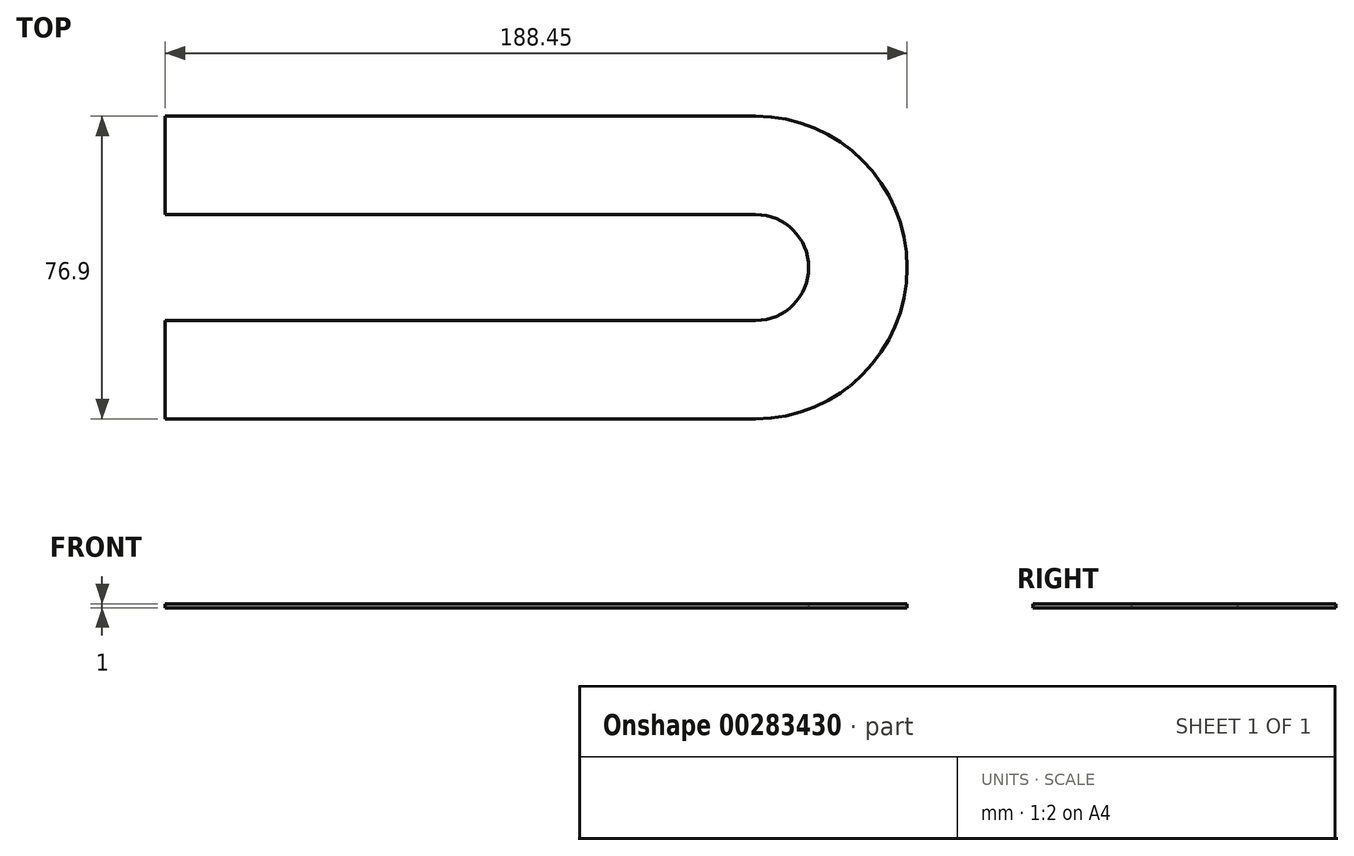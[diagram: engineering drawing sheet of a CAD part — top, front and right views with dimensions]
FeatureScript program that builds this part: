
annotation { "Feature Type Name" : "Feature", "Feature Type Description" : "" }
export const myFeature = defineFeature(function(context is Context, id is Id, definition is map)
    precondition{}
    {
        {
            var Q0;
            Q0=qCreatedBy(makeId("Top.planeOp"),FACE);
            var sketch = newSketch(context, id + "F0", { "sketchPlane" : qUnion([Q0])});
            skCircle(sketch, "E0", {"center": v(0, 0) * mm, "radius": 13.45 * mm});
            skLineSegment(sketch, "E1", {"start": v(0, 13.45) * mm, "end": v(-150, 13.45) * mm});
            skLineSegment(sketch, "E2", {"start": v(-150, 13.45) * mm, "end": v(-150, -13.45) * mm});
            skLineSegment(sketch, "E3", {"start": v(-150, -13.45) * mm, "end": v(0, -13.45) * mm});
            skLineSegment(sketch, "E4", {"start": v(-150, 13.45) * mm, "end": v(-150, 38.45) * mm});
            skLineSegment(sketch, "E5", {"start": v(-150, 38.45) * mm, "end": v(0, 38.45) * mm});
            skLineSegment(sketch, "E6", {"start": v(0, 38.45) * mm, "end": v(0, 13.45) * mm});
            skLineSegment(sketch, "E7", {"start": v(0, -13.45) * mm, "end": v(0, -38.45) * mm});
            skLineSegment(sketch, "E8", {"start": v(0, -38.45) * mm, "end": v(-150, -38.45) * mm});
            skLineSegment(sketch, "E9", {"start": v(-150, -38.45) * mm, "end": v(-150, -13.45) * mm});
            skArc(sketch, "E10", {"start": v(0, -38.45) * mm, "mid": v(38.45, 0) * mm, "end": v(0, 38.45) * mm});
            skSolve(sketch);
        }
        {
            var Q0;
            Q0=makeQuery(id+"F0.imprint","IMPRINT",FACE,{"disambiguationData":[TD([[makeQuery(id+"F0.imprint","IMPRINT",EDGE,{"derivedFrom":sQuery(id+"F0.wireOp",EDGE,"E1")}),-1.0]])]});
            var Q1;
            {var subQ0=sQuery(id+"F0.wireOp",EDGE,"E6");Q1=makeQuery(id+"F0.imprint","IMPRINT",FACE,{"disambiguationData":[TD([[makeQuery(id+"F0.imprint","IMPRINT",EDGE,{"derivedFrom":subQ0}),1.0]])]});}
            var Q2;
            Q2=makeQuery(id+"F0.imprint","IMPRINT",FACE,{"disambiguationData":[TD([[makeQuery(id+"F0.imprint","IMPRINT",EDGE,{"derivedFrom":sQuery(id+"F0.wireOp",EDGE,"E3")}),-1.0]])]});
            extrude(context, id + "F1", {"entities" : qUnion([Q0, Q1, Q2]), "depth" : 1 * mm});
        }
    });
